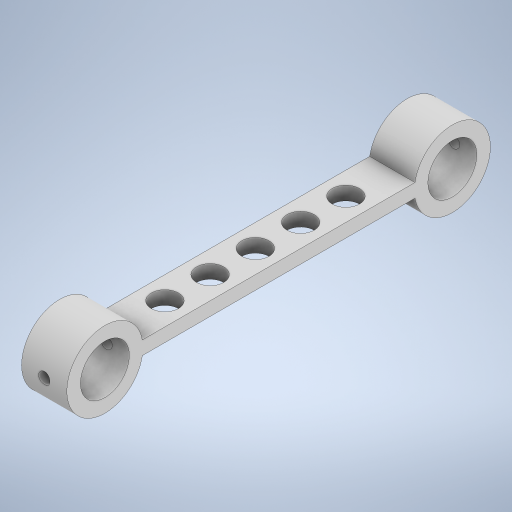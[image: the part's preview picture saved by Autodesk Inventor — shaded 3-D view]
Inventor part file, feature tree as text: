
AUTODESK INVENTOR PART (.ipt)
format: ipt  version: 2024 (Build 280153000, 153)  size: 344,576 bytes
history: native  units: mm
features: other x6, extrude x6, sketch x5, projected_geometry x4
ambient origin geometry x8: Origin, YZ Plane, XZ Plane, XY Plane, X Axis, Y Axis, Z Axis, Center Point
bodies: Body1 (feature_tree)
feature tree (21):
  other  "솔리드1"
  extrude  "돌출1"  Depth=10.8mm
  other  "작업 평면1"
  sketch  "스케치2"
  extrude  "돌출2"  Depth=16.8mm
  extrude  "돌출3"  Depth=10.0mm TaperAngle=0.0deg
  sketch  "스케치4"
  other  "작업 평면3"
  other  "작업 평면4"
  extrude  "돌출4"  Depth=38.4mm
  other  "작업 평면6"
  sketch  "스케치5"
  extrude  "돌출5"  Depth=8.4mm
  extrude  "돌출6"  Depth=3.0mm
  sketch  "스케치1"
  projected_geometry  "투영된 루프1"
  projected_geometry  "투영된 루프2"
  other  "작업 평면5"
  projected_geometry  "투영된 루프3"
  sketch  "스케치6"
  projected_geometry  "투영된 루프4"
